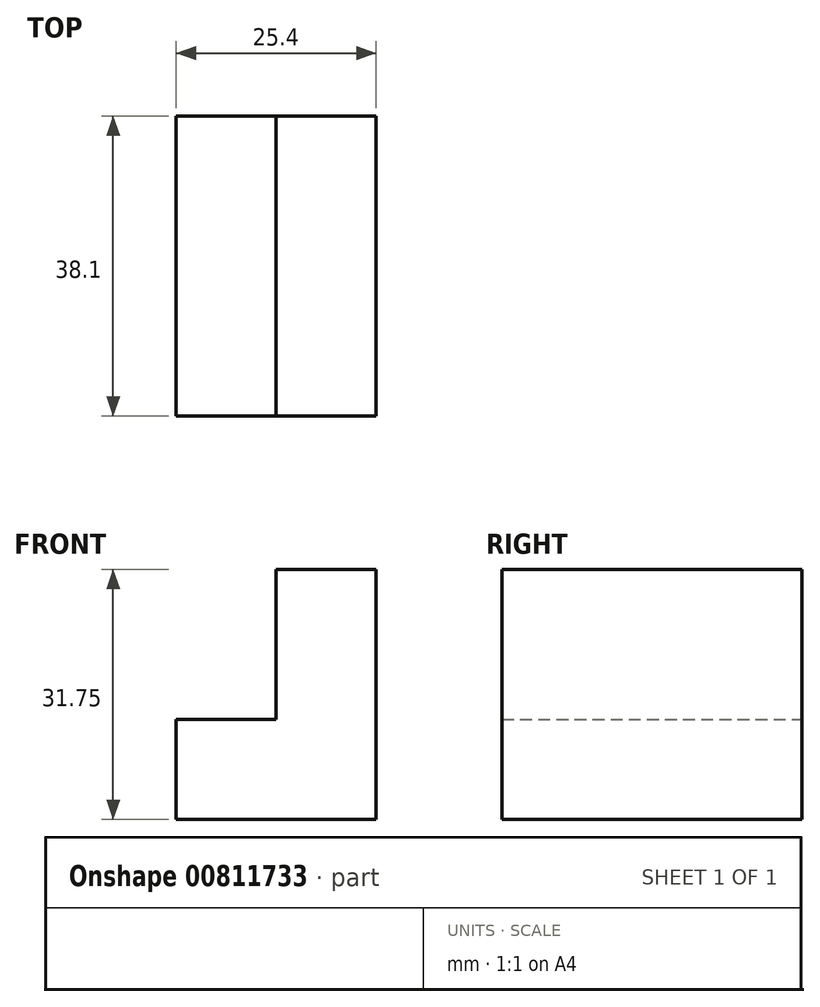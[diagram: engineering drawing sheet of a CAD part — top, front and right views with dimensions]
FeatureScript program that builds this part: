
annotation { "Feature Type Name" : "Feature", "Feature Type Description" : "" }
export const myFeature = defineFeature(function(context is Context, id is Id, definition is map)
    precondition{}
    {
        {
            var Q0;
            Q0=qCreatedBy(makeId("Front.planeOp"),FACE);
            var sketch = newSketch(context, id + "F0", { "sketchPlane" : qUnion([Q0])});
            skLineSegment(sketch, "E0", {"start": v(0, 0) * mm, "end": v(0, 12.7) * mm});
            skLineSegment(sketch, "E1", {"start": v(0, 12.7) * mm, "end": v(12.7, 12.7) * mm});
            skLineSegment(sketch, "E2", {"start": v(12.7, 12.7) * mm, "end": v(12.7, 31.75) * mm});
            skLineSegment(sketch, "E3", {"start": v(12.7, 31.75) * mm, "end": v(25.4, 31.75) * mm});
            skLineSegment(sketch, "E4", {"start": v(25.4, 31.75) * mm, "end": v(25.4, 0) * mm});
            skLineSegment(sketch, "E5", {"start": v(0, 0) * mm, "end": v(25.4, 0) * mm});
            skSolve(sketch);
        }
        {
            var Q0;
            Q0 = qSketchRegion(id + "F0", true);
            extrude(context, id + "F1", {"entities" : qUnion([Q0]), "depth" : 38.1 * mm, "offsetDistance" : 25.4 * mm});
        }
    });
